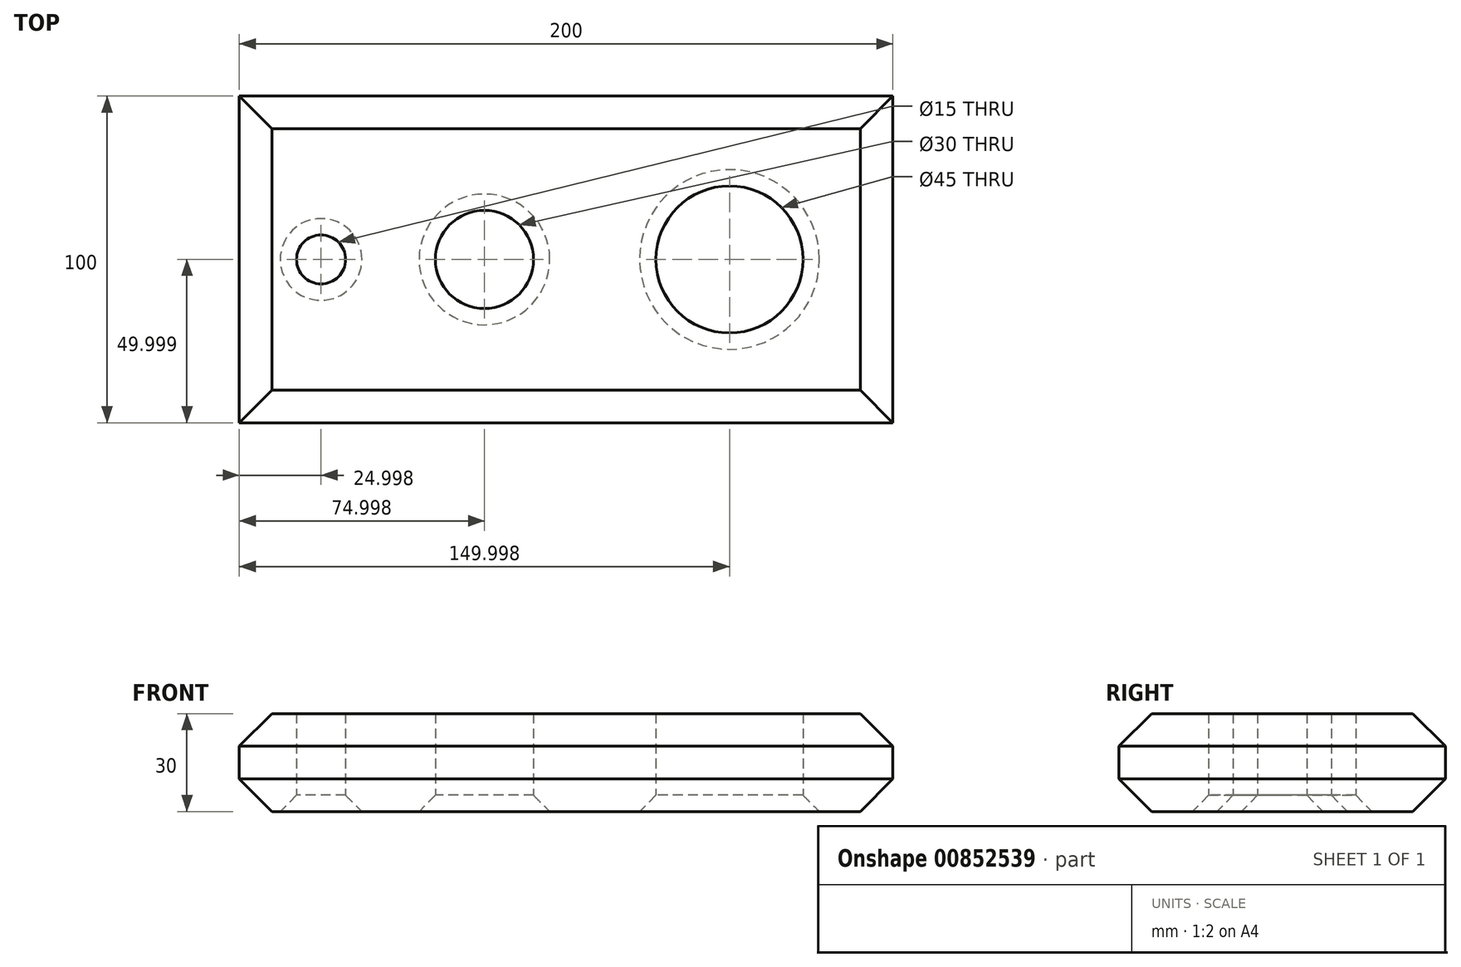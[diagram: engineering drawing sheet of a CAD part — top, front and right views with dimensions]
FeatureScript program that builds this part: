
annotation { "Feature Type Name" : "Feature", "Feature Type Description" : "" }
export const myFeature = defineFeature(function(context is Context, id is Id, definition is map)
    precondition{}
    {
        {
            var Q0;
            Q0=qCreatedBy(makeId("Top.planeOp"),FACE);
            var sketch = newSketch(context, id + "F0", { "sketchPlane" : qUnion([Q0])});
            skLineSegment(sketch, "E0.bottom", {"start": v(-99.71, 57.9) * mm, "end": v(100.29, 57.9) * mm});
            skLineSegment(sketch, "E0.top", {"start": v(-99.71, -42.1) * mm, "end": v(100.29, -42.1) * mm});
            skLineSegment(sketch, "E0.left", {"start": v(-99.71, 57.9) * mm, "end": v(-99.71, -42.1) * mm});
            skLineSegment(sketch, "E0.right", {"start": v(100.29, 57.9) * mm, "end": v(100.29, -42.1) * mm});
            skCircle(sketch, "E1", {"center": v(-74.71, 7.9) * mm, "radius": 7.5 * mm});
            skCircle(sketch, "E2", {"center": v(-24.71, 7.9) * mm, "radius": 15 * mm});
            skCircle(sketch, "E3", {"center": v(50.29, 7.9) * mm, "radius": 22.5 * mm});
            skSolve(sketch);
        }
        {
            var Q0;
            Q0=makeQuery(id+"F0.imprint","IMPRINT",FACE,{"disambiguationData":[TD([[makeQuery(id+"F0.imprint","IMPRINT",EDGE,{"derivedFrom":sQuery(id+"F0.wireOp",EDGE,"E0.bottom")}),-1.0]])]});
            extrude(context, id + "F1", {"entities" : qUnion([Q0]), "depth" : 30 * mm, "offsetDistance" : 25 * mm});
        }
        {
            var Q0;
            Q0=makeQuery(id+"F1.opExtrude","CAP_EDGE",EDGE,{"disambiguationData":[OSD([sQuery(id+"F0.wireOp",EDGE,"E0.bottom")])],"isStart":false});
            var Q1;
            Q1=makeQuery(id+"F1.opExtrude","CAP_EDGE",EDGE,{"disambiguationData":[OSD([sQuery(id+"F0.wireOp",EDGE,"E0.left")])],"isStart":false});
            var Q2;
            Q2=makeQuery(id+"F1.opExtrude","CAP_EDGE",EDGE,{"disambiguationData":[OSD([sQuery(id+"F0.wireOp",EDGE,"E0.top")])],"isStart":false});
            var Q3;
            Q3=makeQuery(id+"F1.opExtrude","CAP_EDGE",EDGE,{"disambiguationData":[OSD([sQuery(id+"F0.wireOp",EDGE,"E0.right")])],"isStart":false});
            chamfer(context, id + "F2", {"entities" : qUnion([Q0, Q1, Q2, Q3]), "chamferType" : ChamferType.OFFSET_ANGLE, "width" : 10 * mm, "oppositeDirection" : false, "angle" : 45 * degree, "tangentPropagation" : true});
        }
        {
            var Q0;
            Q0=makeQuery(id+"F1.opExtrude","CAP_EDGE",EDGE,{"disambiguationData":[OSD([sQuery(id+"F0.wireOp",EDGE,"E0.bottom")])],"isStart":true});
            var Q1;
            Q1=makeQuery(id+"F1.opExtrude","CAP_EDGE",EDGE,{"disambiguationData":[OSD([sQuery(id+"F0.wireOp",EDGE,"E0.left")])],"isStart":true});
            var Q2;
            Q2=makeQuery(id+"F1.opExtrude","CAP_EDGE",EDGE,{"disambiguationData":[OSD([sQuery(id+"F0.wireOp",EDGE,"E0.top")])],"isStart":true});
            var Q3;
            Q3=makeQuery(id+"F1.opExtrude","CAP_EDGE",EDGE,{"disambiguationData":[OSD([sQuery(id+"F0.wireOp",EDGE,"E0.right")])],"isStart":true});
            chamfer(context, id + "F3", {"entities" : qUnion([Q0, Q1, Q2, Q3]), "chamferType" : ChamferType.OFFSET_ANGLE, "width" : 10 * mm, "oppositeDirection" : false, "angle" : 45 * degree, "tangentPropagation" : true});
        }
        {
            var Q0;
            Q0=makeQuery(id+"F1.opExtrude","CAP_EDGE",EDGE,{"disambiguationData":[OSD([sQuery(id+"F0.wireOp",EDGE,"E1")])],"isStart":true});
            var Q1;
            Q1=makeQuery(id+"F1.opExtrude","CAP_EDGE",EDGE,{"disambiguationData":[OSD([sQuery(id+"F0.wireOp",EDGE,"E2")])],"isStart":true});
            var Q2;
            Q2=makeQuery(id+"F1.opExtrude","CAP_EDGE",EDGE,{"disambiguationData":[OSD([sQuery(id+"F0.wireOp",EDGE,"E3")])],"isStart":true});
            chamfer(context, id + "F4", {"entities" : qUnion([Q0, Q1, Q2]), "chamferType" : ChamferType.OFFSET_ANGLE, "width" : 5 * mm, "oppositeDirection" : false, "angle" : 45 * degree, "tangentPropagation" : true});
        }
    });
